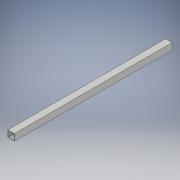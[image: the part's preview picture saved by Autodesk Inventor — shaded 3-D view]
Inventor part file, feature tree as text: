
AUTODESK INVENTOR PART (.ipt)
format: ipt  version: 2017 SP1 (Build 210196100, 196)  size: 98,816 bytes
history: native  units: in
note: dims shown in document units (in); Inventor stores cm internally (conversion verified against a paired STEP export)
features: extrude x1, sketch x1
ambient origin geometry x8: Origin, YZ Plane, XZ Plane, XY Plane, X Axis, Y Axis, Z Axis, Center Point
bodies: Solid1 (feature_tree)
feature tree (2):
  extrude  "Extrusion1"  Depth=1.0in
  sketch  "Sketch1"  dims[d0=1.0in d1=1.0in d2=0.0625in d3=24.0in d4=0.0in]
